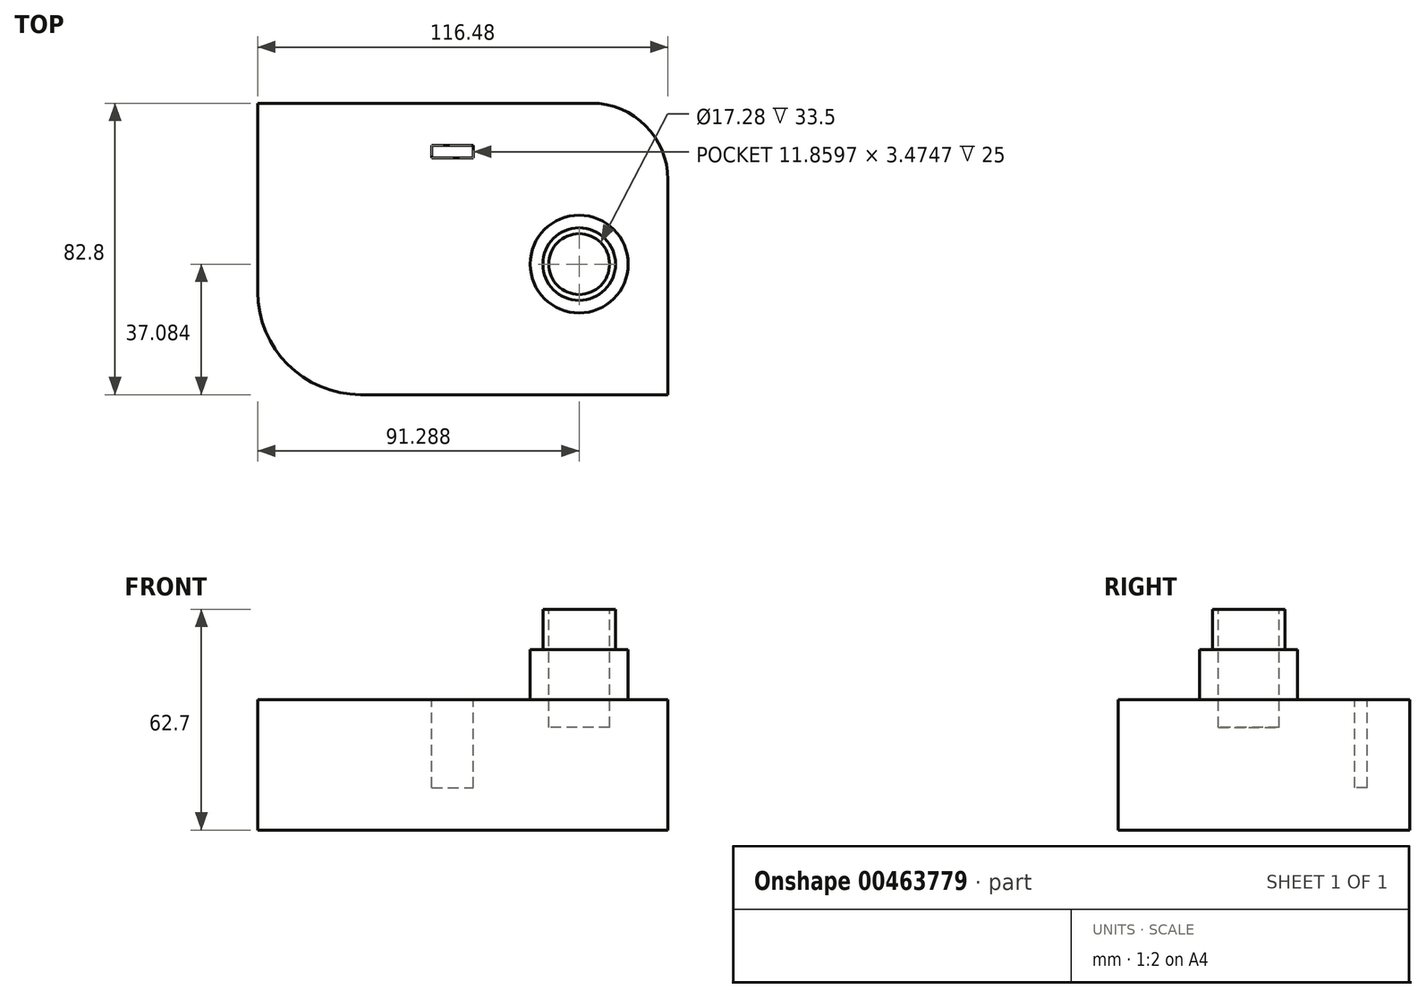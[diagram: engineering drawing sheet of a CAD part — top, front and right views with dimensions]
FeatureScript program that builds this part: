
annotation { "Feature Type Name" : "Feature", "Feature Type Description" : "" }
export const myFeature = defineFeature(function(context is Context, id is Id, definition is map)
    precondition{}
    {
        {
            var Q0;
            Q0=qCreatedBy(makeId("Top.planeOp"),FACE);
            var sketch = newSketch(context, id + "F0", { "sketchPlane" : qUnion([Q0])});
            skLineSegment(sketch, "E0.bottom", {"start": v(-57.73, 31.06) * mm, "end": v(58.75, 31.06) * mm});
            skLineSegment(sketch, "E0.top", {"start": v(-57.73, -51.74) * mm, "end": v(58.75, -51.74) * mm});
            skLineSegment(sketch, "E0.left", {"start": v(-57.73, 31.06) * mm, "end": v(-57.73, -51.74) * mm});
            skLineSegment(sketch, "E0.right", {"start": v(58.75, 31.06) * mm, "end": v(58.75, -51.74) * mm});
            skSolve(sketch);
        }
        {
            var Q0;
            Q0 = qSketchRegion(id + "F0", true);
            extrude(context, id + "F1", {"entities" : qUnion([Q0]), "depth" : 37 * mm});
        }
        {
            var Q0;
            Q0=makeQuery(id+"F1.opExtrude","CAP_FACE",FACE,{"disambiguationData":[OSD([sQuery(id+"F0.wireOp",EDGE,"E0.bottom"),sQuery(id+"F0.wireOp",EDGE,"E0.top"),sQuery(id+"F0.wireOp",EDGE,"E0.left"),sQuery(id+"F0.wireOp",EDGE,"E0.right")])],"isStart":false});
            var sketch = newSketch(context, id + "F2", { "sketchPlane" : qUnion([Q0])});
            skCircle(sketch, "E1", {"center": v(33.56, -14.66) * mm, "radius": 13.9 * mm});
            skPoint(sketch, "E1.first.point", {"position": v(23.57, -4.98) * mm});
            skPoint(sketch, "E1.second.point", {"position": v(46.48, -19.8) * mm});
            skPoint(sketch, "E1.third.point", {"position": v(30.67, -28.26) * mm});
            skSolve(sketch);
        }
        {
            var Q0;
            Q0 = qSketchRegion(id + "F2", true);
            extrude(context, id + "F3", {"entities" : qUnion([Q0]), "operationType" : NewBodyOperationType.ADD, "depth" : 14.2 * mm});
        }
        {
            var Q0;
            Q0=makeQuery(id+"F1.opExtrude","SWEPT_FACE",FACE,{"disambiguationData":[OSD([sQuery(id+"F0.wireOp",EDGE,"E0.bottom")])]});
            var sketch = newSketch(context, id + "F4", { "sketchPlane" : qUnion([Q0])});
            skCircle(sketch, "E2", {"center": v(46.02, 26.27) * mm, "radius": 4.42 * mm});
            skPoint(sketch, "E2.first.point", {"position": v(47.1, 21.99) * mm});
            skPoint(sketch, "E2.second.point", {"position": v(42.86, 29.35) * mm});
            skPoint(sketch, "E2.third.point", {"position": v(41.68, 25.43) * mm});
            skSolve(sketch);
        }
        {
            var Q0;
            Q0=sQuery(id+"F4.wireOp",EDGE,"E2");
            extrude(context, id + "F5", {"bodyType" : ToolBodyType.SURFACE, "surfaceEntities" : qUnion([Q0]), "depth" : 5.1 * mm});
        }
        {
            var Q0;
            Q0=makeQuery(id+"F3.opExtrude","CAP_FACE",FACE,{"disambiguationData":[OSD([sQuery(id+"F2.wireOp",EDGE,"E1")])],"isStart":false});
            var sketch = newSketch(context, id + "F6", { "sketchPlane" : qUnion([Q0])});
            skCircle(sketch, "E3", {"center": v(33.56, -14.66) * mm, "radius": 10.31 * mm});
            skSolve(sketch);
        }
        {
            var Q0;
            Q0 = qSketchRegion(id + "F6", true);
            extrude(context, id + "F7", {"entities" : qUnion([Q0]), "operationType" : NewBodyOperationType.ADD, "depth" : 11.5 * mm});
        }
        {
            var Q0;
            Q0=makeQuery(id+"F7.opExtrude","CAP_FACE",FACE,{"disambiguationData":[OSD([sQuery(id+"F6.wireOp",EDGE,"E3")])],"isStart":false});
            var sketch = newSketch(context, id + "F8", { "sketchPlane" : qUnion([Q0])});
            skCircle(sketch, "E4", {"center": v(33.56, -14.66) * mm, "radius": 8.64 * mm});
            skSolve(sketch);
        }
        {
            var Q0;
            Q0 = qSketchRegion(id + "F8", true);
            extrude(context, id + "F9", {"entities" : qUnion([Q0]), "operationType" : NewBodyOperationType.REMOVE, "oppositeDirection" : true, "depth" : 33.5 * mm});
        }
        {
            var Q0;
            Q0=makeQuery(id+"F1.opExtrude","SWEPT_EDGE",EDGE,{"disambiguationData":[OSD([sQuery(id+"F0.wireOp",EDGE,"E0.bottom"),sQuery(id+"F0.wireOp",EDGE,"E0.right")])]});
            fillet(context, id + "F10", {"entities" : qUnion([Q0]), "radius" : 21.73 * mm, "tangentPropagation" : true, "allowEdgeOverflow" : false});
        }
        {
            var Q0;
            Q0=makeQuery(id+"F1.opExtrude","SWEPT_EDGE",EDGE,{"disambiguationData":[OSD([sQuery(id+"F0.wireOp",EDGE,"E0.top"),sQuery(id+"F0.wireOp",EDGE,"E0.left")])]});
            fillet(context, id + "F11", {"entities" : qUnion([Q0]), "radius" : 29.21 * mm, "tangentPropagation" : true, "allowEdgeOverflow" : false});
        }
        {
            var Q0;
            Q0=makeQuery(id+"F1.opExtrude","CAP_FACE",FACE,{"disambiguationData":[OSD([sQuery(id+"F0.wireOp",EDGE,"E0.bottom"),sQuery(id+"F0.wireOp",EDGE,"E0.top"),sQuery(id+"F0.wireOp",EDGE,"E0.left"),sQuery(id+"F0.wireOp",EDGE,"E0.right")])],"isStart":false});
            var sketch = newSketch(context, id + "F12", { "sketchPlane" : qUnion([Q0])});
            skLineSegment(sketch, "E5.bottom", {"start": v(-8.31, 19) * mm, "end": v(3.55, 19) * mm});
            skLineSegment(sketch, "E5.top", {"start": v(-8.31, 15.53) * mm, "end": v(3.55, 15.53) * mm});
            skLineSegment(sketch, "E5.left", {"start": v(-8.31, 19) * mm, "end": v(-8.31, 15.53) * mm});
            skLineSegment(sketch, "E5.right", {"start": v(3.55, 19) * mm, "end": v(3.55, 15.53) * mm});
            skSolve(sketch);
        }
        {
            var Q0;
            Q0 = qSketchRegion(id + "F12", true);
            extrude(context, id + "F13", {"entities" : qUnion([Q0]), "operationType" : NewBodyOperationType.REMOVE, "oppositeDirection" : true, "depth" : 25 * mm});
        }
    });
